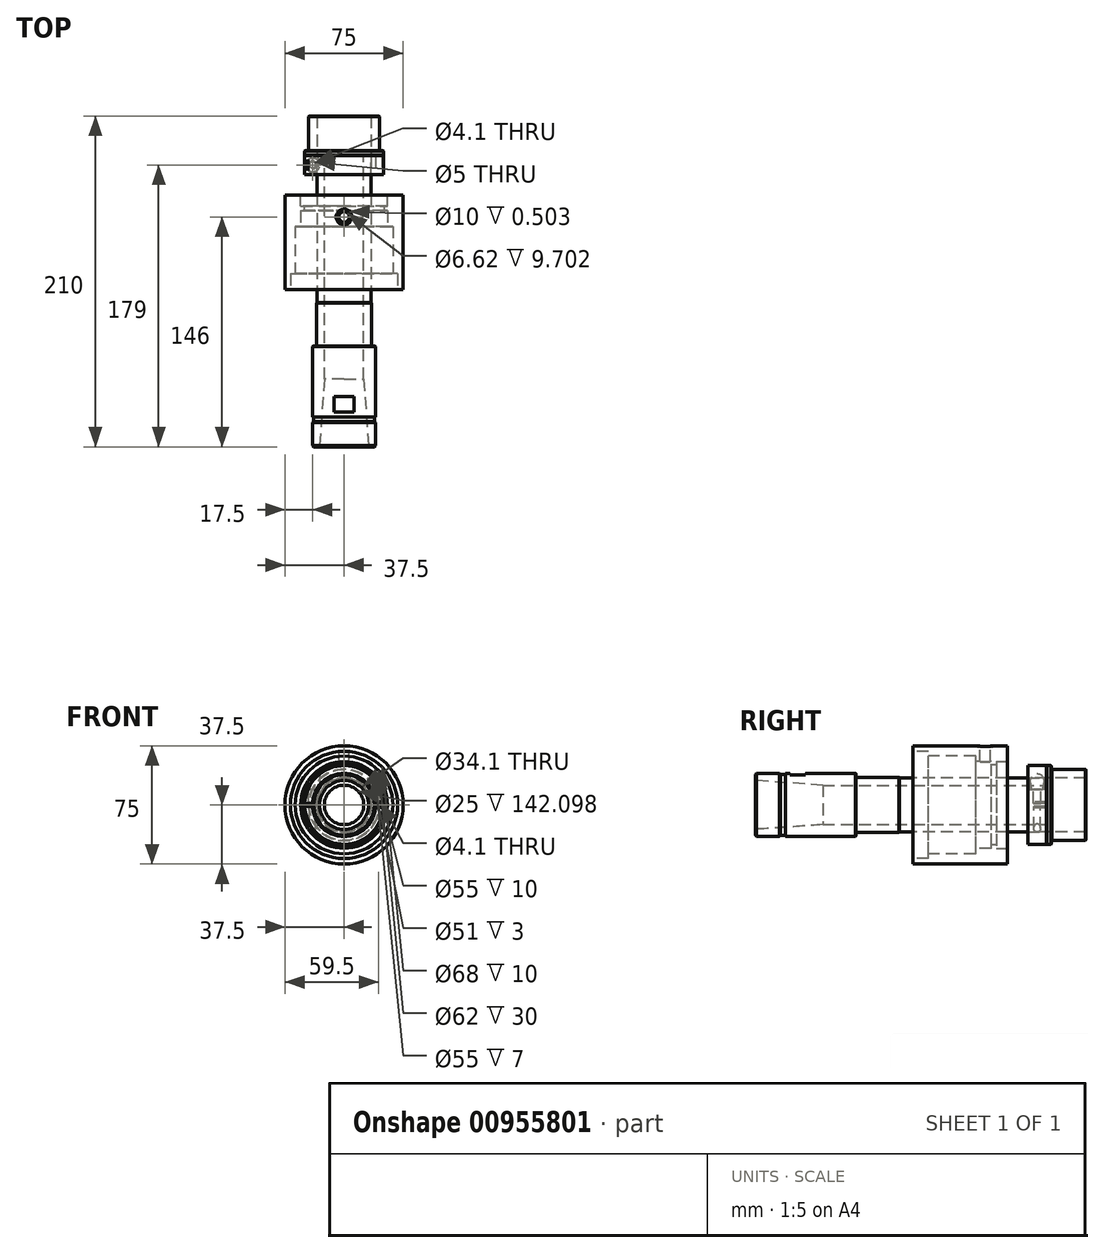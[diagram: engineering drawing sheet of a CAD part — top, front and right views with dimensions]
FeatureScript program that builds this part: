
annotation { "Feature Type Name" : "Feature", "Feature Type Description" : "" }
export const myFeature = defineFeature(function(context is Context, id is Id, definition is map)
    precondition{}
    {
        {
            var Q0;
            Q0=qCreatedBy(makeId("Front.planeOp"),FACE);
            var sketch = newSketch(context, id + "F0", { "sketchPlane" : qUnion([Q0])});
            skCircle(sketch, "E0", {"center": v(0, 0) * mm, "radius": 37.5 * mm});
            skCircle(sketch, "E1", {"center": v(0, 0) * mm, "radius": 25.5 * mm});
            skSolve(sketch);
        }
        {
            var Q0;
            Q0=qSketchRegion(id+"F0",true);
            extrude(context, id + "F1", {"entities" : qUnion([Q0]), "oppositeDirection" : true, "depth" : 60 * mm});
        }
        {
            var Q0;
            Q0=makeQuery(id+"F1.opExtrude","CAP_FACE",FACE,{"disambiguationData":[OSD([sQuery(id+"F0.wireOp",EDGE,"E0"),sQuery(id+"F0.wireOp",EDGE,"E1")])],"isStart":true});
            var sketch = newSketch(context, id + "F2", { "sketchPlane" : qUnion([Q0])});
            skCircle(sketch, "E2", {"center": v(0, 0) * mm, "radius": 34 * mm});
            skSolve(sketch);
        }
        {
            var Q0;
            Q0=qSketchRegion(id+"F2",true);
            extrude(context, id + "F3", {"entities" : qUnion([Q0]), "operationType" : NewBodyOperationType.REMOVE, "oppositeDirection" : true, "depth" : 10 * mm});
        }
        {
            var Q0;
            Q0=makeQuery(id+"F3.boolean.opBoolean","COPY",FACE,{"derivedFrom":makeQuery(id+"F3.opExtrude","CAP_FACE",FACE,{"disambiguationData":[OSD([sQuery(id+"F2.wireOp",EDGE,"E2")])],"isStart":false})});
            var sketch = newSketch(context, id + "F4", { "sketchPlane" : qUnion([Q0])});
            skCircle(sketch, "E3", {"center": v(0, 0) * mm, "radius": 31 * mm});
            skSolve(sketch);
        }
        {
            var Q0;
            Q0=qSketchRegion(id+"F4",true);
            extrude(context, id + "F5", {"entities" : qUnion([Q0]), "operationType" : NewBodyOperationType.REMOVE, "oppositeDirection" : true, "depth" : 30 * mm});
        }
        {
            var Q0;
            Q0=makeQuery(id+"F5.boolean.opBoolean","COPY",FACE,{"derivedFrom":makeQuery(id+"F5.opExtrude","CAP_FACE",FACE,{"disambiguationData":[OSD([sQuery(id+"F4.wireOp",EDGE,"E3")])],"isStart":false})});
            var sketch = newSketch(context, id + "F6", { "sketchPlane" : qUnion([Q0])});
            skCircle(sketch, "E4", {"center": v(0, 0) * mm, "radius": 27.5 * mm});
            skSolve(sketch);
        }
        {
            var Q0;
            Q0=qSketchRegion(id+"F6",true);
            extrude(context, id + "F7", {"entities" : qUnion([Q0]), "operationType" : NewBodyOperationType.REMOVE, "oppositeDirection" : true, "depth" : 10 * mm});
        }
        {
            var Q0;
            Q0=makeQuery(id+"F1.opExtrude","CAP_FACE",FACE,{"disambiguationData":[OSD([sQuery(id+"F0.wireOp",EDGE,"E0"),sQuery(id+"F0.wireOp",EDGE,"E1")])],"isStart":false});
            var sketch = newSketch(context, id + "F8", { "sketchPlane" : qUnion([Q0])});
            skCircle(sketch, "E5", {"center": v(0, 0) * mm, "radius": 27.5 * mm});
            skSolve(sketch);
        }
        {
            var Q0;
            Q0=qSketchRegion(id+"F8",true);
            extrude(context, id + "F9", {"entities" : qUnion([Q0]), "operationType" : NewBodyOperationType.REMOVE, "oppositeDirection" : true, "depth" : 7 * mm});
        }
        {
            var Q0;
            Q0=qCreatedBy(makeId("Top.planeOp"),FACE);
            cPlane(context, id + "F10", {"entities" : qUnion([Q0]), "cplaneType" : CPlaneType.OFFSET, "offset" : (75 / 2) * mm, "width" : 150 * mm, "height" : 150 * mm});
        }
        {
            var Q0;
            Q0=qCreatedBy(id+"F10.planeOp",FACE);
            var sketch = newSketch(context, id + "F11", { "sketchPlane" : qUnion([Q0])});
            skLineSegment(sketch, "E6", {"start": v(0, 0) * mm, "end": v(0, 60) * mm, "construction": true});
            skPoint(sketch, "E7", {"position": v(0, 46) * mm});
            skCircle(sketch, "E8", {"center": v(0, 46) * mm, "radius": 5 * mm});
            skSolve(sketch);
        }
        {
            var Q0;
            Q0=qSketchRegion(id+"F11",true);
            extrude(context, id + "F12", {"entities" : qUnion([Q0]), "operationType" : NewBodyOperationType.REMOVE, "oppositeDirection" : true, "depth" : .5 * mm});
        }
        {
            var Q0;
            Q0=makeQuery(id+"F12.boolean.opBoolean","COPY",FACE,{"derivedFrom":makeQuery(id+"F12.opExtrude","CAP_FACE",FACE,{"disambiguationData":[OSD([sQuery(id+"F11.wireOp",EDGE,"E8")])],"isStart":false})});
            var sketch = newSketch(context, id + "F13", { "sketchPlane" : qUnion([Q0])});
            skPoint(sketch, "E9", {"position": v(0, 46) * mm});
            skSolve(sketch);
        }
        {
            var Q0;
            Q0=sQuery(id+"F13.wireOp",VERTEX,"E9");
            var Q1;
            Q1=makeQuery(id+"F1.opExtrude","SWEPT_BODY",BODY,{"disambiguationData":[OSD([sQuery(id+"F0.wireOp",EDGE,"E0"),sQuery(id+"F0.wireOp",EDGE,"E1")])]});
            hole(context, id + "F14", {"style" : HoleStyle.SIMPLE, "endStyle" : HoleEndStyle.BLIND, "holeDiameter" : 6.62 * mm, "holeDepth" : 12 * mm, "locations" : qUnion([Q0]), "scope" : qUnion([Q1])});
        }
        {
            var Q0;
            Q0=qCreatedBy(makeId("Front.planeOp"),FACE);
            cPlane(context, id + "F15", {"entities" : qUnion([Q0]), "cplaneType" : CPlaneType.OFFSET, "offset" : 100 * mm, "width" : 150 * mm, "height" : 150 * mm});
        }
        {
            var Q0;
            Q0=qCreatedBy(id+"F15.planeOp",FACE);
            var sketch = newSketch(context, id + "F16", { "sketchPlane" : qUnion([Q0])});
            skCircle(sketch, "E10", {"center": v(0, 0) * mm, "radius": 20 * mm});
            skSolve(sketch);
        }
        {
            var Q0;
            Q0=qSketchRegion(id+"F16",true);
            extrude(context, id + "F17", {"entities" : qUnion([Q0]), "oppositeDirection" : true, "depth" : 16 * mm});
        }
        {
            var Q0;
            Q0=makeQuery(id+"F17.opExtrude","CAP_FACE",FACE,{"disambiguationData":[OSD([sQuery(id+"F16.wireOp",EDGE,"E10")])],"isStart":false});
            var sketch = newSketch(context, id + "F18", { "sketchPlane" : qUnion([Q0])});
            skCircle(sketch, "E11", {"center": v(0, 0) * mm, "radius": 19.25 * mm});
            skSolve(sketch);
        }
        {
            var Q0;
            Q0=qSketchRegion(id+"F18",true);
            extrude(context, id + "F19", {"entities" : qUnion([Q0]), "operationType" : NewBodyOperationType.ADD, "depth" : 3 * mm});
        }
        {
            var Q0;
            Q0=makeQuery(id+"F19.opExtrude","CAP_FACE",FACE,{"disambiguationData":[OSD([sQuery(id+"F18.wireOp",EDGE,"E11")])],"isStart":false});
            var sketch = newSketch(context, id + "F20", { "sketchPlane" : qUnion([Q0])});
            skCircle(sketch, "E12", {"center": v(0, 0) * mm, "radius": 20 * mm});
            skSolve(sketch);
        }
        {
            var Q0;
            Q0=qSketchRegion(id+"F20",true);
            extrude(context, id + "F21", {"entities" : qUnion([Q0]), "operationType" : NewBodyOperationType.ADD, "depth" : 45 * mm});
        }
        {
            var Q0;
            Q0=makeQuery(id+"F21.opExtrude","CAP_FACE",FACE,{"disambiguationData":[OSD([sQuery(id+"F20.wireOp",EDGE,"E12")])],"isStart":false});
            var sketch = newSketch(context, id + "F22", { "sketchPlane" : qUnion([Q0])});
            skCircle(sketch, "E13", {"center": v(0, 0) * mm, "radius": 17.5 * mm});
            skSolve(sketch);
        }
        {
            var Q0;
            Q0=qSketchRegion(id+"F22",true);
            extrude(context, id + "F23", {"entities" : qUnion([Q0]), "operationType" : NewBodyOperationType.ADD, "depth" : 27.5 * mm});
        }
        {
            var Q0;
            Q0=makeQuery(id+"F23.opExtrude","CAP_FACE",FACE,{"disambiguationData":[OSD([sQuery(id+"F22.wireOp",EDGE,"E13")])],"isStart":false});
            var sketch = newSketch(context, id + "F24", { "sketchPlane" : qUnion([Q0])});
            skCircle(sketch, "E14", {"center": v(0, 0) * mm, "radius": 17 * mm});
            skSolve(sketch);
        }
        {
            var Q0;
            Q0=qSketchRegion(id+"F24",true);
            extrude(context, id + "F25", {"entities" : qUnion([Q0]), "operationType" : NewBodyOperationType.ADD, "depth" : 140 * mm});
        }
        {
            var Q0;
            Q0=makeQuery(id+"F25.opExtrude","CAP_FACE",FACE,{"disambiguationData":[OSD([sQuery(id+"F24.wireOp",EDGE,"E14")])],"isStart":false});
            var sketch = newSketch(context, id + "F26", { "sketchPlane" : qUnion([Q0])});
            skCircle(sketch, "E15", {"center": v(0, 0) * mm, "radius": 15.88 * mm});
            skSolve(sketch);
        }
        {
            var Q0;
            Q0=qSketchRegion(id+"F26",true);
            extrude(context, id + "F27", {"entities" : qUnion([Q0]), "operationType" : NewBodyOperationType.ADD, "depth" : 50 * mm});
        }
        {
            var Q0;
            Q0=makeQuery(id+"F17.opExtrude","CAP_FACE",FACE,{"disambiguationData":[OSD([sQuery(id+"F16.wireOp",EDGE,"E10")])],"isStart":true});
            var sketch = newSketch(context, id + "F28", { "sketchPlane" : qUnion([Q0])});
            skCircle(sketch, "E16", {"center": v(0, 0) * mm, "radius": 15.5 * mm});
            skSolve(sketch);
        }
        {
            var Q0;
            Q0=qSketchRegion(id+"F28",true);
            extrude(context, id + "F29", {"entities" : qUnion([Q0]), "operationType" : NewBodyOperationType.REMOVE, "oppositeDirection" : true, "depth" : 50 * mm, "hasDraft" : true, "draftAngle" : 4 * degree, "draftPullDirection" : true});
        }
        {
            var Q0;
            Q0=makeQuery(id+"F27.opExtrude","CAP_FACE",FACE,{"disambiguationData":[OSD([sQuery(id+"F26.wireOp",EDGE,"E15")])],"isStart":false});
            var sketch = newSketch(context, id + "F30", { "sketchPlane" : qUnion([Q0])});
            skCircle(sketch, "E17", {"center": v(0, 0) * mm, "radius": 12.5 * mm});
            skSolve(sketch);
        }
        {
            var Q0;
            Q0=qSketchRegion(id+"F30",true);
            extrude(context, id + "F31", {"entities" : qUnion([Q0]), "operationType" : NewBodyOperationType.REMOVE, "endBound" : BoundingType.THROUGH_ALL, "oppositeDirection" : true, "depth" : 25 * mm});
        }
        {
            var Q0;
            Q0=makeQuery(id+"F1.opExtrude","CAP_FACE",FACE,{"disambiguationData":[OSD([sQuery(id+"F0.wireOp",EDGE,"E0"),sQuery(id+"F0.wireOp",EDGE,"E1")])],"isStart":false});
            cPlane(context, id + "F32", {"entities" : qUnion([Q0]), "cplaneType" : CPlaneType.OFFSET, "offset" : 25 * mm, "width" : 150 * mm, "height" : 150 * mm});
        }
        {
            var Q0;
            Q0=qCreatedBy(id+"F32.planeOp",FACE);
            var sketch = newSketch(context, id + "F33", { "sketchPlane" : qUnion([Q0])});
            skCircle(sketch, "E18", {"center": v(0, 0) * mm, "radius": 25 * mm});
            skSolve(sketch);
        }
        {
            var Q0;
            Q0=qSketchRegion(id+"F33",true);
            extrude(context, id + "F34", {"entities" : qUnion([Q0]), "depth" : 3 * mm});
        }
        {
            var Q0;
            Q0=makeQuery(id+"F34.opExtrude","CAP_FACE",FACE,{"disambiguationData":[OSD([sQuery(id+"F33.wireOp",EDGE,"E18")])],"isStart":false});
            var sketch = newSketch(context, id + "F35", { "sketchPlane" : qUnion([Q0])});
            skCircle(sketch, "E19", {"center": v(0, 0) * mm, "radius": 22.5 * mm});
            skSolve(sketch);
        }
        {
            var Q0;
            Q0=qSketchRegion(id+"F35",true);
            extrude(context, id + "F36", {"entities" : qUnion([Q0]), "operationType" : NewBodyOperationType.ADD, "depth" : 22 * mm});
        }
        {
            var Q0;
            Q0=makeQuery(id+"F34.opExtrude","CAP_FACE",FACE,{"disambiguationData":[OSD([sQuery(id+"F33.wireOp",EDGE,"E18")])],"isStart":true});
            var sketch = newSketch(context, id + "F37", { "sketchPlane" : qUnion([Q0])});
            skCircle(sketch, "E20", {"center": v(0, 0) * mm, "radius": 17.05 * mm});
            skSolve(sketch);
        }
        {
            var Q0;
            Q0=qSketchRegion(id+"F37",true);
            extrude(context, id + "F38", {"entities" : qUnion([Q0]), "operationType" : NewBodyOperationType.REMOVE, "endBound" : BoundingType.UP_TO_NEXT, "oppositeDirection" : true, "depth" : 25 * mm});
        }
        {
            var Q0;
            Q0=makeQuery(id+"F34.opExtrude","SWEPT_FACE",FACE,{"disambiguationData":[OSD([sQuery(id+"F33.wireOp",EDGE,"E18")])]});
            var Q1;
            Q1=makeQuery(id+"F36.opExtrude","SWEPT_FACE",FACE,{"disambiguationData":[OSD([sQuery(id+"F35.wireOp",EDGE,"E19")])]});
            var Q2;
            Q2=makeQuery(id+"F38.boolean.opBoolean","COPY",FACE,{"derivedFrom":makeQuery(id+"F38.opExtrude","SWEPT_FACE",FACE,{"disambiguationData":[OSD([sQuery(id+"F37.wireOp",EDGE,"E20")])]})});
            chamfer(context, id + "F39", {"entities" : qUnion([Q0, Q1, Q2]), "width" : .25 * mm, "tangentPropagation" : true});
        }
        {
            var Q0;
            Q0=makeQuery(id+"F17.opExtrude","SWEPT_FACE",FACE,{"disambiguationData":[OSD([sQuery(id+"F16.wireOp",EDGE,"E10")])]});
            var Q1;
            Q1=makeQuery(id+"FgnukjYGfaEQPH9_2.opExtrude","SWEPT_FACE",FACE,{"disambiguationData":[OSD([sQuery(id+"Fpo6LL3ajyrS8uz_2.wireOp",EDGE,"ZPJ78Gsf-ZMfG-ODoI-Mz2S-bczQQD3Yarib")])]});
            var Q2;
            Q2=makeQuery(id+"FODl2dEUZz75cc0_5.opExtrude","CAP_FACE",FACE,{"disambiguationData":[OSD([sQuery(id+"F1eT8sYVKhEZkZg_5.wireOp",EDGE,"IbQkoDR8-f8DR-9itt-bgPZ-ocWSv4ODY6js")])],"isStart":false});
            chamfer(context, id + "F40", {"entities" : qUnion([Q0, Q1, Q2]), "width" : .75 * mm, "tangentPropagation" : true});
        }
        {
            var Q0;
            Q0=qCreatedBy(makeId("Right.planeOp"),FACE);
            var sketch = newSketch(context, id + "F41", { "sketchPlane" : qUnion([Q0])});
            skLineSegment(sketch, "E21.bottom", {"start": v(-68, 21) * mm, "end": v(-78, 21) * mm});
            skLineSegment(sketch, "E21.top", {"start": v(-68, 19) * mm, "end": v(-78, 19) * mm});
            skLineSegment(sketch, "E21.left", {"start": v(-68, 21) * mm, "end": v(-68, 19) * mm});
            skLineSegment(sketch, "E21.right", {"start": v(-78, 21) * mm, "end": v(-78, 19) * mm});
            skPoint(sketch, "E21.middle", {"position": v(-73, 20) * mm});
            skSolve(sketch);
        }
        {
            var Q0;
            Q0=qSketchRegion(id+"F41",true);
            extrude(context, id + "F42", {"entities" : qUnion([Q0]), "operationType" : NewBodyOperationType.REMOVE, "endBound" : BoundingType.SYMMETRIC, "depth" : 15 * mm});
        }
        {
            var Q0;
            Q0=makeQuery(id+"F23.opExtrude","CAP_EDGE",EDGE,{"disambiguationData":[OSD([sQuery(id+"F22.wireOp",EDGE,"E13")])],"isStart":false});
            var Q1;
            Q1=makeQuery(id+"F21.opExtrude","CAP_EDGE",EDGE,{"disambiguationData":[OSD([sQuery(id+"F20.wireOp",EDGE,"E12")])],"isStart":false});
            var Q2;
            Q2=makeQuery(id+"F25.opExtrude","CAP_EDGE",EDGE,{"disambiguationData":[OSD([sQuery(id+"F24.wireOp",EDGE,"E14")])],"isStart":false});
            var Q3;
            Q3=makeQuery(id+"F27.opExtrude","CAP_FACE",FACE,{"disambiguationData":[OSD([sQuery(id+"F26.wireOp",EDGE,"E15")])],"isStart":false});
            chamfer(context, id + "F43", {"entities" : qUnion([Q0, Q1, Q2, Q3]), "width" : .25 * mm, "tangentPropagation" : true});
        }
        {
            var Q0;
            Q0=makeQuery(id+"F34.opExtrude","CAP_FACE",FACE,{"disambiguationData":[OSD([sQuery(id+"F33.wireOp",EDGE,"E18")])],"isStart":true});
            var sketch = newSketch(context, id + "F44", { "sketchPlane" : qUnion([Q0])});
            skCircle(sketch, "E22", {"center": v(0, 0) * mm, "radius": 25 * mm});
            skCircle(sketch, "E23", {"center": v(0, 0) * mm, "radius": 17.05 * mm});
            skSolve(sketch);
        }
        {
            var Q0;
            Q0=qSketchRegion(id+"F44",true);
            extrude(context, id + "F45", {"entities" : qUnion([Q0]), "depth" : 12 * mm});
        }
        {
            var Q0;
            Q0=qCreatedBy(makeId("Top.planeOp"),FACE);
            cPlane(context, id + "F46", {"entities" : qUnion([Q0]), "cplaneType" : CPlaneType.OFFSET, "offset" : 10 * mm, "width" : 150 * mm, "height" : 150 * mm});
        }
        {
            var Q0;
            Q0=qCreatedBy(id+"F46.planeOp",FACE);
            var sketch = newSketch(context, id + "F47", { "sketchPlane" : qUnion([Q0])});
            skPoint(sketch, "E24", {"position": v(-20, 79) * mm});
            skCircle(sketch, "E25", {"center": v(-20, 79) * mm, "radius": 4.5 * mm});
            skSolve(sketch);
        }
        {
            var Q0;
            Q0=qSketchRegion(id+"F47",true);
            var Q1;
            Q1=makeQuery(id+"F45.opExtrude","SWEPT_FACE",FACE,{"disambiguationData":[OSD([sQuery(id+"F44.wireOp",EDGE,"E22")])]});
            extrude(context, id + "F48", {"entities" : qUnion([Q0]), "operationType" : NewBodyOperationType.REMOVE, "endBound" : BoundingType.UP_TO_SURFACE, "endBoundEntityFace" : qUnion([Q1]), "depth" : 25 * mm});
        }
        {
            var Q0;
            Q0=makeQuery(id+"F48.boolean.opBoolean","COPY",FACE,{"derivedFrom":makeQuery(id+"F48.opExtrude","CAP_FACE",FACE,{"disambiguationData":[OSD([sQuery(id+"F47.wireOp",EDGE,"E25")])],"isStart":true})});
            var sketch = newSketch(context, id + "F49", { "sketchPlane" : qUnion([Q0])});
            skPoint(sketch, "E26", {"position": v(-20, 79) * mm});
            skSolve(sketch);
        }
        {
            var Q0;
            Q0=sQuery(id+"F49.wireOp",VERTEX,"E26");
            var Q1;
            Q1=makeQuery(id+"F45.opExtrude","SWEPT_BODY",BODY,{"disambiguationData":[OSD([sQuery(id+"F44.wireOp",EDGE,"E22"),sQuery(id+"F44.wireOp",EDGE,"E23")])]});
            hole(context, id + "F50", {"style" : HoleStyle.SIMPLE, "endStyle" : HoleEndStyle.THROUGH, "standardTappedOrClearance" : lookupTablePath({ "standard" : "ISO", "engagement" : "75%", "pitch" : "0.9 mm", "size" : "M5", "type" : "Tapped" }), "standardBlindInLast" : lookupTablePath({ "standard" : "ISO", "engagement" : "75%", "pitch" : "0.9 mm", "size" : "M5", "type" : "Tapped" }), "holeDiameter" : 4.1 * mm, "locations" : qUnion([Q0]), "scope" : qUnion([Q1]), "isTappedThrough" : true, "showTappedDepth" : true});
        }
        {
            var Q0;
            Q0=sQuery(id+"F49.wireOp",VERTEX,"E26");
            var Q1;
            Q1=makeQuery(id+"F45.opExtrude","SWEPT_BODY",BODY,{"disambiguationData":[OSD([sQuery(id+"F44.wireOp",EDGE,"E22"),sQuery(id+"F44.wireOp",EDGE,"E23")])]});
            hole(context, id + "F51", {"style" : HoleStyle.SIMPLE, "endStyle" : HoleEndStyle.BLIND, "standardTappedOrClearance" : lookupTablePath({ "standard" : "ISO", "size" : "5", "type" : "Drilled" }), "standardBlindInLast" : lookupTablePath({ "standard" : "ISO", "size" : "5", "type" : "Drilled" }), "holeDiameter" : 5 * mm, "holeDepth" : 9 * mm, "locations" : qUnion([Q0]), "scope" : qUnion([Q1])});
        }
        {
            var Q0;
            Q0=makeQuery(id+"F45.opExtrude","CAP_FACE",FACE,{"disambiguationData":[OSD([sQuery(id+"F44.wireOp",EDGE,"E22"),sQuery(id+"F44.wireOp",EDGE,"E23")])],"isStart":false});
            var sketch = newSketch(context, id + "F52", { "sketchPlane" : qUnion([Q0])});
            skLineSegment(sketch, "E27", {"start": v(0, 0) * mm, "end": v(-25, 0) * mm, "construction": true});
            skLineSegment(sketch, "E28.bottom", {"start": v(-16.5, 1) * mm, "end": v(-25.5, 1) * mm});
            skLineSegment(sketch, "E28.top", {"start": v(-16.5, -1) * mm, "end": v(-25.5, -1) * mm});
            skLineSegment(sketch, "E28.left", {"start": v(-16.5, 1) * mm, "end": v(-16.5, -1) * mm});
            skLineSegment(sketch, "E28.right", {"start": v(-25.5, 1) * mm, "end": v(-25.5, -1) * mm});
            skPoint(sketch, "E28.middle", {"position": v(-21, 0) * mm});
            skSolve(sketch);
        }
        {
            var Q0;
            Q0=qSketchRegion(id+"F52",true);
            extrude(context, id + "F53", {"entities" : qUnion([Q0]), "operationType" : NewBodyOperationType.REMOVE, "oppositeDirection" : true, "depth" : 12 * mm});
        }
        {
            var Q0;
            Q0=makeQuery(id+"F45.opExtrude","CAP_FACE",FACE,{"disambiguationData":[OSD([sQuery(id+"F44.wireOp",EDGE,"E22"),sQuery(id+"F44.wireOp",EDGE,"E23")])],"isStart":false});
            var sketch = newSketch(context, id + "F54", { "sketchPlane" : qUnion([Q0])});
            skLineSegment(sketch, "E29", {"start": v(0, 0) * mm, "end": v(25, 0) * mm, "construction": true});
            skPoint(sketch, "E30", {"position": v(0, 0) * mm});
            skPoint(sketch, "E31", {"position": v(22, 0) * mm});
            skSolve(sketch);
        }
        {
            var Q0;
            Q0=sQuery(id+"F54.wireOp",VERTEX,"E31");
            var Q1;
            Q1=makeQuery(id+"F45.opExtrude","SWEPT_BODY",BODY,{"disambiguationData":[OSD([sQuery(id+"F44.wireOp",EDGE,"E22"),sQuery(id+"F44.wireOp",EDGE,"E23")])]});
            hole(context, id + "F55", {"style" : HoleStyle.SIMPLE, "endStyle" : HoleEndStyle.THROUGH, "standardTappedOrClearance" : lookupTablePath({ "standard" : "ISO", "engagement" : "75%", "pitch" : "0.9 mm", "size" : "M5", "type" : "Tapped" }), "standardBlindInLast" : lookupTablePath({ "standard" : "ISO", "engagement" : "75%", "pitch" : "0.9 mm", "size" : "M5", "type" : "Tapped" }), "holeDiameter" : 4.1 * mm, "locations" : qUnion([Q0]), "scope" : qUnion([Q1]), "isTappedThrough" : true, "showTappedDepth" : true});
        }
    });
